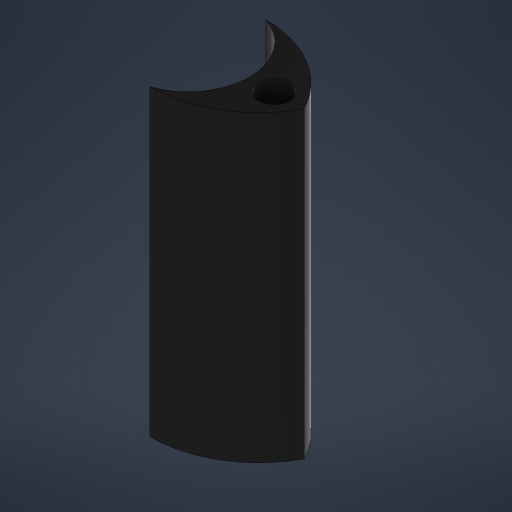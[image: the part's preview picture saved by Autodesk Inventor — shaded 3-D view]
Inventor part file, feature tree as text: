
AUTODESK INVENTOR PART (.ipt)
format: ipt  version: 2023.5 (Build 275446000, 446)  size: 211,456 bytes
history: native  units: mm
features: extrude x1, sketch x1
ambient origin geometry x8: Origin, YZ Plane, XZ Plane, XY Plane, X Axis, Y Axis, Z Axis, Center Point
bodies: Volumenkörper1 (feature_tree)
feature tree (2):
  extrude  "Extrusion1"  [1 undecoded]
  sketch  "Skizze1"  dims[d0=47.0mm d1=0.0mm]
note: 1 required parameter value undecoded (feature->parameter linkage not recoverable at this tier; creation-order binding heuristic only, values carry confidence <= 0.55)
